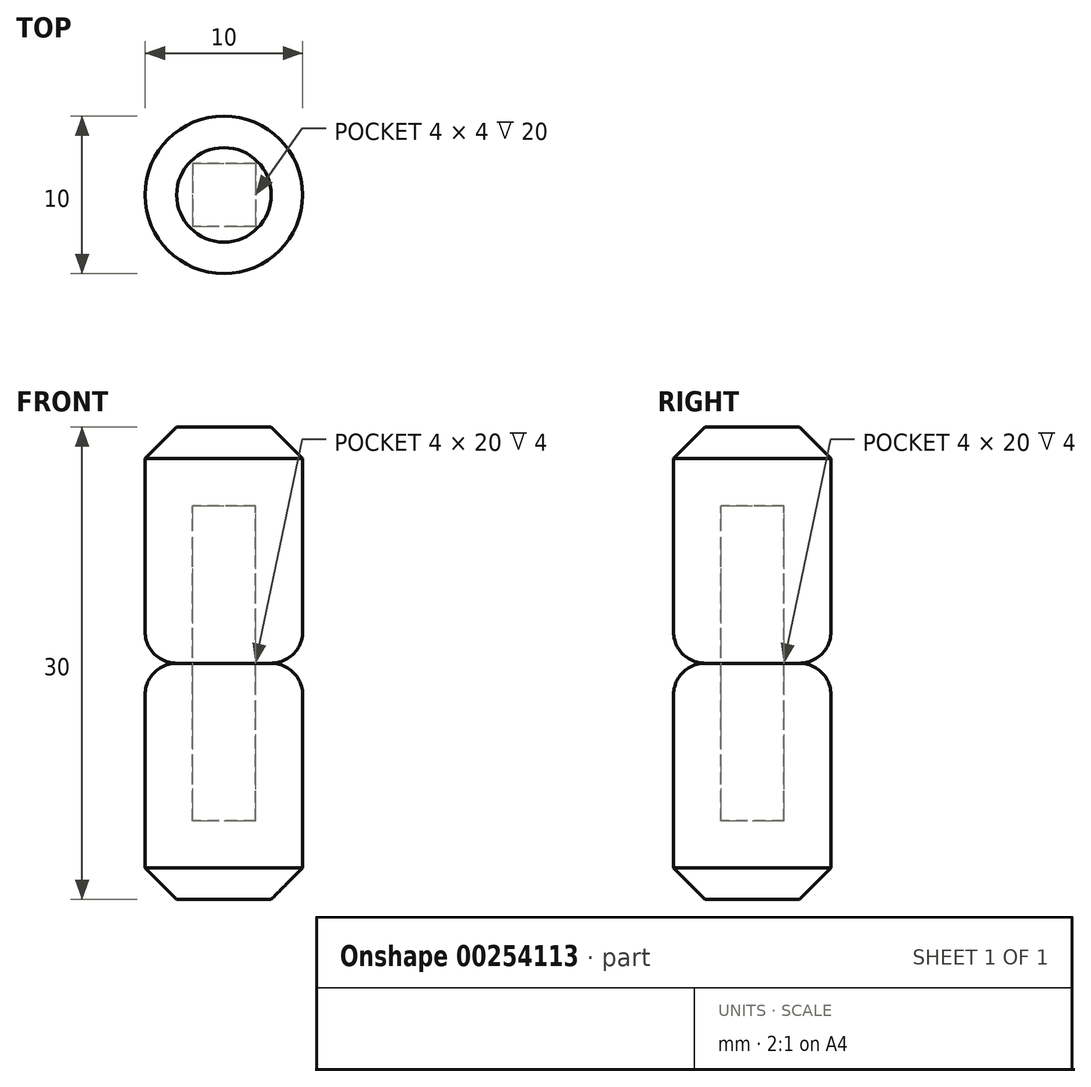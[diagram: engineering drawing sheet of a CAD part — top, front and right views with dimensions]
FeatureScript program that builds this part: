
annotation { "Feature Type Name" : "Feature", "Feature Type Description" : "" }
export const myFeature = defineFeature(function(context is Context, id is Id, definition is map)
    precondition{}
    {
        {
            var Q0;
            Q0=qCreatedBy(makeId("Top.planeOp"),FACE);
            var sketch = newSketch(context, id + "F0", { "sketchPlane" : qUnion([Q0])});
            skCircle(sketch, "E0", {"center": v(0, 0) * mm, "radius": 5 * mm});
            skSolve(sketch);
        }
        {
            var Q0;
            Q0 = qSketchRegion(id + "F0", true);
            extrude(context, id + "F1", {"entities" : qUnion([Q0]), "depth" : 15 * mm});
        }
        {
            var Q0;
            Q0=makeQuery(id+"F1.opExtrude","CAP_FACE",FACE,{"disambiguationData":[OSD([sQuery(id+"F0.wireOp",EDGE,"E0")])],"isStart":false});
            var sketch = newSketch(context, id + "F2", { "sketchPlane" : qUnion([Q0])});
            skLineSegment(sketch, "E1.bottom", {"start": v(2, 2) * mm, "end": v(-2, 2) * mm});
            skLineSegment(sketch, "E1.top", {"start": v(2, -2) * mm, "end": v(-2, -2) * mm});
            skLineSegment(sketch, "E1.left", {"start": v(2, 2) * mm, "end": v(2, -2) * mm});
            skLineSegment(sketch, "E1.right", {"start": v(-2, 2) * mm, "end": v(-2, -2) * mm});
            skPoint(sketch, "E1.middle", {"position": v(0, 0) * mm});
            skSolve(sketch);
        }
        {
            var Q0;
            Q0 = qSketchRegion(id + "F2", true);
            extrude(context, id + "F3", {"entities" : qUnion([Q0]), "operationType" : NewBodyOperationType.REMOVE, "oppositeDirection" : true, "depth" : 10 * mm});
        }
        {
            var Q0;
            Q0=makeQuery(id+"F1.opExtrude","CAP_EDGE",EDGE,{"disambiguationData":[OSD([sQuery(id+"F0.wireOp",EDGE,"E0")])],"isStart":false});
            fillet(context, id + "F4", {"entities" : qUnion([Q0]), "radius" : 2 * mm, "tangentPropagation" : true, "allowEdgeOverflow" : false});
        }
        {
            var Q0;
            Q0=makeQuery(id+"F1.opExtrude","CAP_EDGE",EDGE,{"disambiguationData":[OSD([sQuery(id+"F0.wireOp",EDGE,"E0")])],"isStart":true});
            chamfer(context, id + "F5", {"entities" : qUnion([Q0]), "width" : 2 * mm, "tangentPropagation" : true});
        }
        {
            var Q0;
            Q0=makeQuery(id+"F1.opExtrude","SWEPT_BODY",BODY,{"disambiguationData":[OSD([sQuery(id+"F0.wireOp",EDGE,"E0")])]});
            var Q1;
            Q1=makeQuery(id+"F1.opExtrude","CAP_FACE",FACE,{"disambiguationData":[OSD([sQuery(id+"F0.wireOp",EDGE,"E0")])],"isStart":false});
            mirror(context, id + "F6", {"operationType" : NewBodyOperationType.ADD, "entities" : qUnion([Q0]), "mirrorPlane" : qUnion([Q1])});
        }
    });
